# Revit family: Table-Casual-Naughtone-TraceTblLarge_Circular
name_source: partatom
category: Furniture
revit_build: Autodesk Revit 2015 (Build: 20150704_0715(x64)
units: mm (PartAtom-declared; Revit-internal decimal feet)

## types (2) — shared parameters
Assembly Code = E2020200
AssetType = Movable
BIMObjectName = Table-Casual-Naughtone-TraceTblLrge_Circular
BarCode = 0.000000
Category = 40.50.21.58 : Occasional Tables
CodePerformance = FISP Certified; ISO14001 Certified
Color = White
ComponentDescription = Sold by the likes of MOMA in New York, the trace table range is simply a modern classic that speaks for itself. Suffice to say the immaculate hand made steel frame and repetition of shapes make trace an exquisitely balanced form.
Constituents = Cold drawn mild steel, Various top options
DurationUnit = Years
ExpectedLife = 15-20
Finish = Polyster powder coat; various top finishes available
Keynote = 40.50.21.58
Manufacturer = Naughtone
ManufacturerDetailsUK = 201 Pannal Business Park, Station Road, Harrogate, HG3 1JL
ModelReference = Trace Circular Table Large
NBSReference = 40.50.21.58
Name = Table-Casual-Naughtone-TraceTblLrge_Circular
NominalHeight = 750 mm  [stored 2.46063 ft]
Product URL = http://www.naughtone.com
ProductInformation = http://www.naughtone.com
ReplacementCost = 0.00
Shape = Circular
SustainabilityPerformance = 44.8% reusable content. 100% recycled & recyclable content
URL = http://www.naughtone.com
Uniclass2015 = 40.50.21.58
Version = 2
WarrantyDescription = 5 Year Warranty
WarrantyDurationLabor = 5
WarrantyDurationParts = 5
WarrantyDurationUnit = Years
_current revision = 2
_distributed by = www.bimbox.co.uk
zero-valued in all types: Cost, SerialNumber, TagNumber, _BIMspec_GUID

## per-type parameters (varying)
| type | Description | NominalLength | NominalWidth | Size | Type Comments | TypeName |
| TRA-1200-DIA | Trace Circular Table 1200mm | 1200 mm  [stored 3.93701 ft] | 1200 mm  [stored 3.93701 ft] | 1200mmx1200mmx750mm | 1200x1200x750 | 1200mmx1200mmx750mm, Trace Table Large |
| TRA-1400-DIA | Trace Circular Table 1400mm | 1400 mm  [stored 4.59318 ft] | 1400 mm  [stored 4.59318 ft] | 1400mmx1400mmx750mm | 1400x1400x750 | 1400mmx1400mmx750mm, Trace Table Large |

note: column(s) folded — value = type name in every type: AssetIdentifier, Model, ModelNumber

note: [stored X ft] marks values corroborated as IEEE doubles in the binary element streams (Revit-internal decimal feet)

## geometry (parser evidence)
native form markers: Sweep x3
no freeform markers — native parametric forms only
